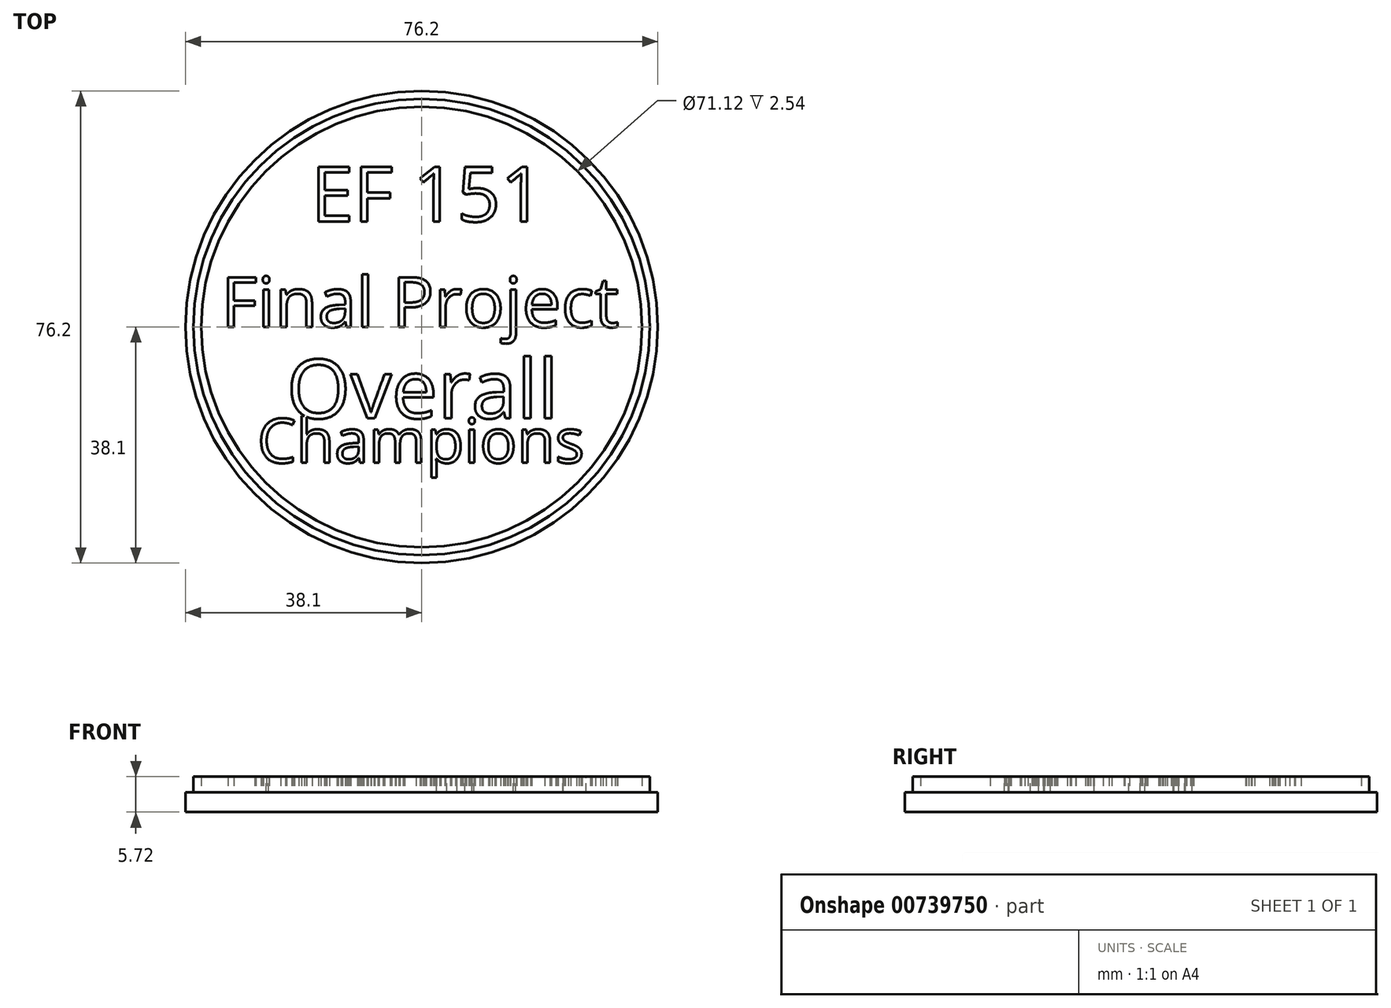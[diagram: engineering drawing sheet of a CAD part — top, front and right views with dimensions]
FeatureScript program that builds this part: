
annotation { "Feature Type Name" : "Feature", "Feature Type Description" : "" }
export const myFeature = defineFeature(function(context is Context, id is Id, definition is map)
    precondition{}
    {
        {
            var Q0;
            Q0=qCreatedBy(makeId("Top.planeOp"),FACE);
            var sketch = newSketch(context, id + "F0", { "sketchPlane" : qUnion([Q0])});
            skCircle(sketch, "E0", {"center": v(0, 0) * mm, "radius": 38.1 * mm});
            skSolve(sketch);
        }
        {
            var Q0;
            Q0=makeQuery(id+"F0.imprint","IMPRINT",FACE,{"disambiguationData":[TD([[makeQuery(id+"F0.imprint","IMPRINT",EDGE,{"derivedFrom":sQuery(id+"F0.wireOp",EDGE,"E0")}),1.0]])]});
            extrude(context, id + "F1", {"entities" : qUnion([Q0]), "depth" : 3.17 * mm, "offsetDistance" : 25.4 * mm});
        }
        {
            var Q0;
            Q0=makeQuery(id+"F1.opExtrude","CAP_FACE",FACE,{"disambiguationData":[OSD([sQuery(id+"F0.wireOp",EDGE,"E0")])],"isStart":false});
            var sketch = newSketch(context, id + "F2", { "sketchPlane" : qUnion([Q0])});
            skCircle(sketch, "E1", {"center": v(0, 0) * mm, "radius": 36.83 * mm});
            skCircle(sketch, "E2", {"center": v(0, 0) * mm, "radius": 35.56 * mm});
            skSolve(sketch);
        }
        {
            var Q0;
            Q0=makeQuery(id+"F2.imprint","IMPRINT",FACE,{"disambiguationData":[TD([[makeQuery(id+"F2.imprint","IMPRINT",EDGE,{"derivedFrom":sQuery(id+"F2.wireOp",EDGE,"E1")}),1.0]])]});
            extrude(context, id + "F3", {"entities" : qUnion([Q0]), "operationType" : NewBodyOperationType.ADD, "depth" : 2.54 * mm, "offsetDistance" : 25.4 * mm});
        }
        {
            var Q0;
            Q0=makeQuery(id+"F3.boolean.opBoolean","SPLIT",FACE,{"disambiguationData":[TD([makeQuery(id+"F3.opExtrude","SWEPT_FACE",FACE,{"disambiguationData":[OSD([sQuery(id+"F2.wireOp",EDGE,"E2")])]})])],"derivedFrom":makeQuery(id+"F1.opExtrude","CAP_FACE",FACE,{"disambiguationData":[OSD([sQuery(id+"F0.wireOp",EDGE,"E0")])],"isStart":false})});
            var sketch = newSketch(context, id + "F4", { "sketchPlane" : qUnion([Q0])});
            skText(sketch, "E3", { "text": "EF 151", "fontName": "OpenSans-Regular.ttf"});
            skText(sketch, "E4", { "text": "Final Project", "fontName": "OpenSans-Regular.ttf"});
            skText(sketch, "E5", { "text": "Overall", "fontName": "OpenSans-Regular.ttf"});
            skText(sketch, "E6", { "text": "Champions", "fontName": "OpenSans-Regular.ttf"});
            const initialGuessF4  = {"E3": [-0.01783, 0.01703, 1, 0, 0.00888], "E4": [-0.03232, 0, 1, 0, 0.00809], "E5": [-0.0218, -0.01474, 1, 0, 0.00954], "E6": [-0.0265, -0.02193, 1, 0, 0.00718]};
            skSetInitialGuess(sketch, initialGuessF4);
            skSolve(sketch);
        }
        {
            var Q0;
            Q0=qSketchRegion(id+"F4",true);
            extrude(context, id + "F5", {"entities" : qUnion([Q0]), "operationType" : NewBodyOperationType.ADD, "depth" : 2.54 * mm, "offsetDistance" : 25.4 * mm});
        }
    });
